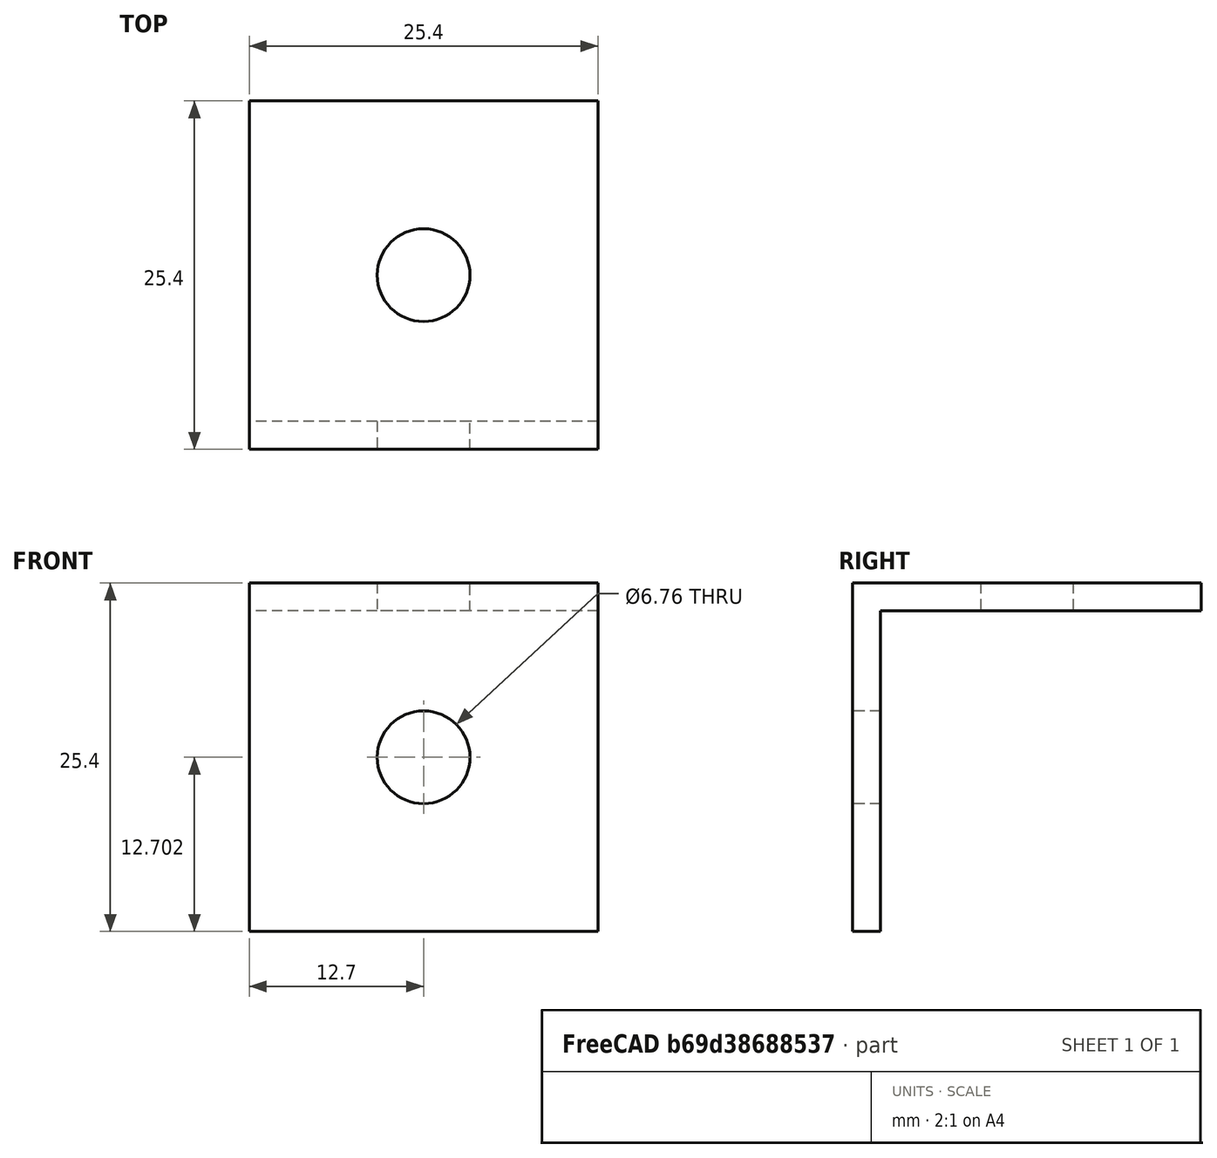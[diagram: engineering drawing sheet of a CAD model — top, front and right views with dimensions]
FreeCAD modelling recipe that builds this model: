
FCSTD DOCUMENT  (FreeCAD 1.0R39285 (Git))
Label: FEM
License: All rights reserved
LicenseURL: https://en.wikipedia.org/wiki/All_rights_reserved
objects: Sketcher::SketchObject×2, PartDesign::Pad×2, PartDesign::Body×1, Fem::FemSolverObjectPython×1, App::MaterialObjectPython×1, Fem::ConstraintFixed×1, Fem::ConstraintForce×1, Fem::FemAnalysis×1
note: 11 computed .brp shape members not serialized (recipe doc carries the construction recipe); baked Part::Feature solids carry a one-line shape summary decoded from their .brp

FEATURE [Sketcher::SketchObject] Sketch
  ArcFitTolerance = 1e-06
  AttachmentSupport = -> [XY_Plane]
  FullyConstrained = true
  MakeInternals = false
  MapMode = 5
  sketch-geometry (5):
    g0: LineSegment StartX=-12.7 StartY=12.7 StartZ=0 EndX=-12.7 EndY=-12.7 EndZ=0
    g1: LineSegment StartX=-12.7 StartY=-12.7 StartZ=0 EndX=12.7 EndY=-12.7 EndZ=0
    g2: LineSegment StartX=12.7 StartY=-12.7 StartZ=0 EndX=12.7 EndY=12.7 EndZ=0
    g3: LineSegment StartX=12.7 StartY=12.7 StartZ=0 EndX=-12.7 EndY=12.7 EndZ=0
    g4: Circle CenterX=0 CenterY=0 CenterZ=0 NormalX=0 NormalY=0 NormalZ=1 AngleXU=0 Radius=3.3782
  constraints (13):
    c: Coincident(g0,g1)
    c: Coincident(g1,g2)
    c: Coincident(g2,g3)
    c: Coincident(g3,g0)
    c: Vertical(g0)
    c: Vertical(g2)
    c: Horizontal(g1)
    c: Horizontal(g3)
    c: Coincident(g4,g-1)
    c: Symmetric(g0,g1,g4)
    c: Equal(g3,g0)
    c: DistanceX(g3,g3) = 25.4
    c: Diameter(g4) = 6.7564
FEATURE [PartDesign::Pad] Pad
  Direction = (0,0,1)
  Length = 2.032
  Length2 = 10
  Profile = -> Sketch
  ReferenceAxis = -> Sketch [N_Axis]
  Refine = true
  Suppressed = false
  Type = 0
FEATURE [Sketcher::SketchObject] Sketch001
  ArcFitTolerance = 1e-06
  AttachmentSupport = -> [Pad]
  ExternalGeometry = -> [Pad]
  FullyConstrained = true
  MakeInternals = false
  MapMode = 5
  Placement = pos=(0,-12.7,0) rot=(1,0,0;1.5708rad)
  sketch-geometry (5):
    g0: LineSegment StartX=-12.7 StartY=2.032 StartZ=0 EndX=-12.7 EndY=-23.368 EndZ=0
    g1: LineSegment StartX=-12.7 StartY=-23.368 StartZ=0 EndX=12.7 EndY=-23.368 EndZ=0
    g2: LineSegment StartX=12.7 StartY=-23.368 StartZ=0 EndX=12.7 EndY=2.032 EndZ=0
    g3: LineSegment StartX=12.7 StartY=2.032 StartZ=0 EndX=-12.7 EndY=2.032 EndZ=0
    g4: Circle CenterX=-1.1e-15 CenterY=-10.668 CenterZ=0 NormalX=0 NormalY=0 NormalZ=1 AngleXU=0 Radius=3.3782
  constraints (12):
    c: Coincident(g0,g1)
    c: Coincident(g1,g2)
    c: Coincident(g2,g3)
    c: Coincident(g3,g0)
    c: Vertical(g0)
    c: Vertical(g2)
    c: Horizontal(g1)
    c: Coincident(g0,g-3)
    c: Coincident(g2,g-3)
    c: Equal(g3,g0)
    c: Diameter(g4) = 6.7564
    c: Symmetric(g0,g1,g4)
FEATURE [PartDesign::Pad] Pad001
  BaseFeature = -> Pad
  Direction = (0,-1,2e-16)
  Length = 2.032
  Length2 = 10
  Profile = -> Sketch001
  ReferenceAxis = -> Sketch001 [N_Axis]
  Refine = true
  Reversed = true
  Suppressed = false
  Type = 0
FEATURE [PartDesign::Body] Body
  AllowCompound = false
  Group = -> [Sketch,Pad,Sketch001,Pad001]
  Origin = -> Origin
  Tip = -> Pad001
FEATURE [Fem::FemSolverObjectPython] SolverCcxTools  # FEM object (typed FeaturePython)
  AnalysisType = 0
  BeamReducedIntegration = true
  BeamShellResultOutput3D = true
  BucklingFactors = 1
  EigenmodeHighLimit = 1000000
  EigenmodeLowLimit = 0
  EigenmodesCount = 10
  GeometricalNonlinearity = 0
  IterationsControlParameterCutb = 0.25,0.5,0.75,0.85,,,1.5,
  IterationsControlParameterIter = 4,8,9,200,10,400,,200,,
  IterationsControlParameterTimeUse = false
  IterationsMaximum = 2000
  IterationsUserDefinedIncrementations = false
  IterationsUserDefinedTimeStepLength = false
  MaterialNonlinearity = 0
  MatrixSolverType = 0
  ModelSpace = 0
  OutputFrequency = 1
  SplitInputWriter = false
  ThermoMechSteadyState = true
  ThermoMechType = 0
  TimeEnd = 1
  TimeInitialStep = 1
  TimeMaximumStep = 1
  TimeMinimumStep = 1e-05
FEATURE [App::MaterialObjectPython] MaterialSolid  # material (typed FeaturePython)
  Category = 0
  Material = Author=Uwe Stöhr,AuthorAndLicense=CC-BY-3.0,CardName=PLA-Generic,Density=1.24e-06 kg/mm^3,+12 more (map truncated)
  UUID = 93861244-fbbe-41a9-a7e0-aeed53abd782
FEATURE [Fem::ConstraintFixed] ConstraintFixed
  NormalDirection = (1,0,-1e-16)
  Normals = (9) [(-1,0,0),(1,-2.69422e-32,-1.22465e-16),(-1,5.38845e-32,2.44929e-16),(-1,0,0),(1,-2.69422e-32,-1.22465e-16),(-1,5.38845e-32,2.44929e-16),(-1,0,0),+2 more]
  Points = (9) [(3.3782,-10.668,-10.668),(-3.3782,-10.668,-10.668),(3.3782,-10.668,-10.668),(3.3782,-11.684,-10.668),(-3.3782,-11.684,-10.668),+4 more]
  References = -> [Pad001]
  Suppressed = false
FEATURE [Fem::ConstraintForce] ConstraintForce
  DirectionVector = (0,0,-1)
  Force = 50000
  NormalDirection = (0,0,1)
  Normals = (16) [(0,0,1),(0,0,1),(0,0,1),(0,0,1),(0,0,1),(0,0,1),(0,0,1),(0,0,1),(0,0,1),(0,0,1),(0,0,1),(0,0,1),(0,0,1),(0,0,1),(0,0,1),(0,0,1)]
  Points = (16) [(-12.7,-12.7,2.032),(-4.23333,-12.7,2.032),(4.23333,-12.7,2.032),(12.7,-12.7,2.032),(-12.7,-4.23333,2.032),(-4.23333,-4.23333,2.032),+10 more]
  References = -> [Pad001]
  Reversed = true
  Suppressed = false
FEATURE [Fem::FemAnalysis] Analysis
  Group = -> [SolverCcxTools,MaterialSolid,ConstraintFixed,ConstraintForce]
